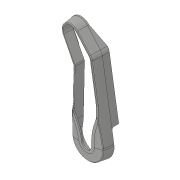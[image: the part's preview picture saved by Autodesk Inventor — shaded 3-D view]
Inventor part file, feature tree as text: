
AUTODESK INVENTOR PART (.ipt)
format: ipt  version: 2019.4 (Build 234330000, 330)  size: 665,600 bytes
history: native  units: mm
features: sketch x14, other x8, extrude x7, reference x5, fillet x4, sweep x2, chamfer x2, hole x2, loft x1
ambient origin geometry x8: Origin, YZ Plane, XZ Plane, XY Plane, X Axis, Y Axis, Z Axis, Center Point
bodies: Body1 (feature_tree)
feature tree (45):
  other  "ソリッド1"
  extrude  "押し出し1"  Depth=2.0mm TaperAngle=0.0deg
  extrude  "押し出し2"  Depth=13.4mm TaperAngle=0.0deg
  extrude  "押し出し7"  Depth=8.0mm TaperAngle=0.0deg
  extrude  "押し出し8"  Depth=3.0mm TaperAngle=0.0deg
  extrude  "押し出し9"  Depth=2.0mm TaperAngle=0.0deg
  sketch  "スケッチ10"
  sketch  "スケッチ11"
  sweep  "スイープ1"
  sweep  "スイープ2"
  sketch  "スケッチ14"
  sketch  "スケッチ15"
  other  "作業平面1"
  chamfer  "面取り4"  Distance=3.95mm
  chamfer  "面取り6"  Distance=2.0mm
  loft  "ロフト1"
  fillet  "フィレット3"  Radius=2.0mm
  fillet  "フィレット4"  Radius=65.0mm
  extrude  "押し出し11"  TaperAngle=0.0deg  [1 undecoded]
  extrude  "押し出し10"  Depth=2.0mm
  other  "作業平面2"
  sketch  "スケッチ20"
  hole  "穴1"  [1 undecoded]
  hole  "穴2"  [1 undecoded]
  fillet  "フィレット6"  [1 undecoded]
  fillet  "フィレット7"  Radius=2.0mm
  sketch  "スケッチ2"
  sketch  "スケッチ7"
  sketch  "スケッチ8"
  sketch  "スケッチ9"
  reference  "参照14"
  sketch  "3D スケッチ1"
  sketch  "スケッチ12"
  sketch  "スケッチ13"
  reference  "参照15"
  sketch  "3D スケッチ2"
  sketch  "スケッチ16"
  other  "エッジ1"
  reference  "参照24"
  reference  "参照26"
  reference  "参照27"
  parser-record x1  (decoder bookkeeping rows leaked as tree rows — omitted from the tree; the rows remain in map.json)
  other  "UPPER_LEG_ASM.iam"
  other  "UPPER_LEG_OUTER_FRAME:1"
  other  "SERVO_BOTTOM_SPACER:1"
note: 4 required parameter values undecoded (feature->parameter linkage not recoverable at this tier; creation-order binding heuristic only, values carry confidence <= 0.55)
note: 1 file-system path scrubbed to <path> (originals preserved in map.json)
